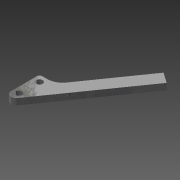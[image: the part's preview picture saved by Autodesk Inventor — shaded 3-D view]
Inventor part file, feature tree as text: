
AUTODESK INVENTOR PART (.ipt)
format: ipt  version: 2015 (Build 190159000, 159)  size: 111,104 bytes
history: native  units: mm
features: other x3, fillet x3, sketch x2, hole x1
ambient origin geometry x8: Origin, YZ Plane, XZ Plane, XY Plane, X Axis, Y Axis, Z Axis, Center Point
bodies: Body1 (feature_tree)
feature tree (9):
  other  "Bryła1"
  other  "Powierzchnia1"
  hole  "Otwór1"  [1 undecoded]
  fillet  "Zaokrąglenie2"  Radius=35.0mm
  fillet  "Zaokrąglenie3"  Radius=50.0mm
  fillet  "Zaokrąglenie4"  Radius=25.0mm
  sketch  "Szkic1"
  other  "Płyta1"
  sketch  "Szkic2"
note: 1 required parameter value undecoded (feature->parameter linkage not recoverable at this tier; creation-order binding heuristic only, values carry confidence <= 0.55)
